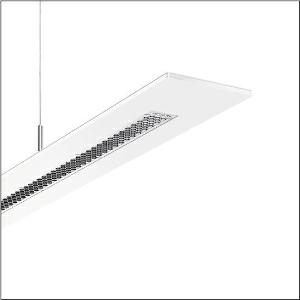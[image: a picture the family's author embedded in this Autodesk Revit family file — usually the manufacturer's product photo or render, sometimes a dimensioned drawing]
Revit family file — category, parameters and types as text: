
# Revit family: arktika_r__21_5mb2512l30830_74ae
name_source: partatom
category: Lighting Fixtures
units: mm (PartAtom-declared; Revit-internal decimal feet)

## family parameters
Cut with Voids When Loaded = No
Host = Face
Light Source = No
Part Type = Normal
Room Calculation Point = No
Round Connector Dimension = Use Diameter
Shared = No

## types (1)
- Arktika® 21 (1 x LED 3000K / CRI = 80 (unbekannt), 3670 lm, 3000K)
    Apparent Load = 31 VA
    CIE Flux Codes = 81 100 100 79 100
    Color Rendering = 80
    Color Temperature = 3000K
    Default Elevation = 1800 mm
    Description = Arktika® 21, office luminaire, primary anti-glare with honeycomb louvre, of plastic, aluminium vaporised, highly specular, light emission: direct/indirect distribution, primary light characteristic: symmetric, installation type: suspended mounting, LED, rated luminous flux: 3.670lm, luminous efficacy: 120lm/W, light colour: 830, colour temperature: 3000K, control gear: ECG, with terminal, 3-pole, mains connection: 220..240V, AC, 50/60Hz, rated input power: 31W, housing, of aluminium, powder-coated, traffic white (RAL 9016), 1-length, length: 1.250mm, width: 120mm, height: 8mm, protection rating (complete): IP20, insulation class (complete): insulation class II (safety insulation), certification: CE, packaging unit: 1 piece
    Height = 8 mm  [stored 0.0262467 ft]
    Lamp = 1 x LED 3000K / CRI >= 80 (unbekannt)
    Lamp Light Flux = 3670 lm
    Lamp count = 1
    Length = 1250 mm
    Luminous efficacy = 120 lm/W
    Manufacturer = Siteco
    ModVariant = No
    Model = 5MB2512L30830
    Mounting Place = Ceiling
    Mounting Type = Pendant
    Number of Poles = 1
    OnlyDefault = Yes
    Power Factor = 1
    Product Name = Arktika® 21
    Product group = office luminaire | ceiling pendant
    ProductGroupID = 902
    Protection Class = Protection class II
    Protection Degree = IP 20
    RLX_Detail_Level = 1
    RLX_Emergency_Light_Flux = 0 lm
    RLX_Emergency_Type = 0
    RLX_Emergency_Type_DB = No
    RlxData = <blob elided: 36029 chars, md5=f0229d48>
    Socket = socket
    Standby Power = 0 W
    System Light Flux = 3670 lm
    System Power = 31 W
    Type Comments = Product without accessories
    Type Image = l_1006128.jpg
    URL = http://relux.com
    VarID = ---
    Voltage = 0 V
    Weight = 0.00 kg
    Width = 120 mm

note: [stored X ft] marks values corroborated as IEEE doubles in the binary element streams (Revit-internal decimal feet)

## geometry (parser evidence)
native form markers: Blend x4, Sweep x11
no freeform markers — native parametric forms only
